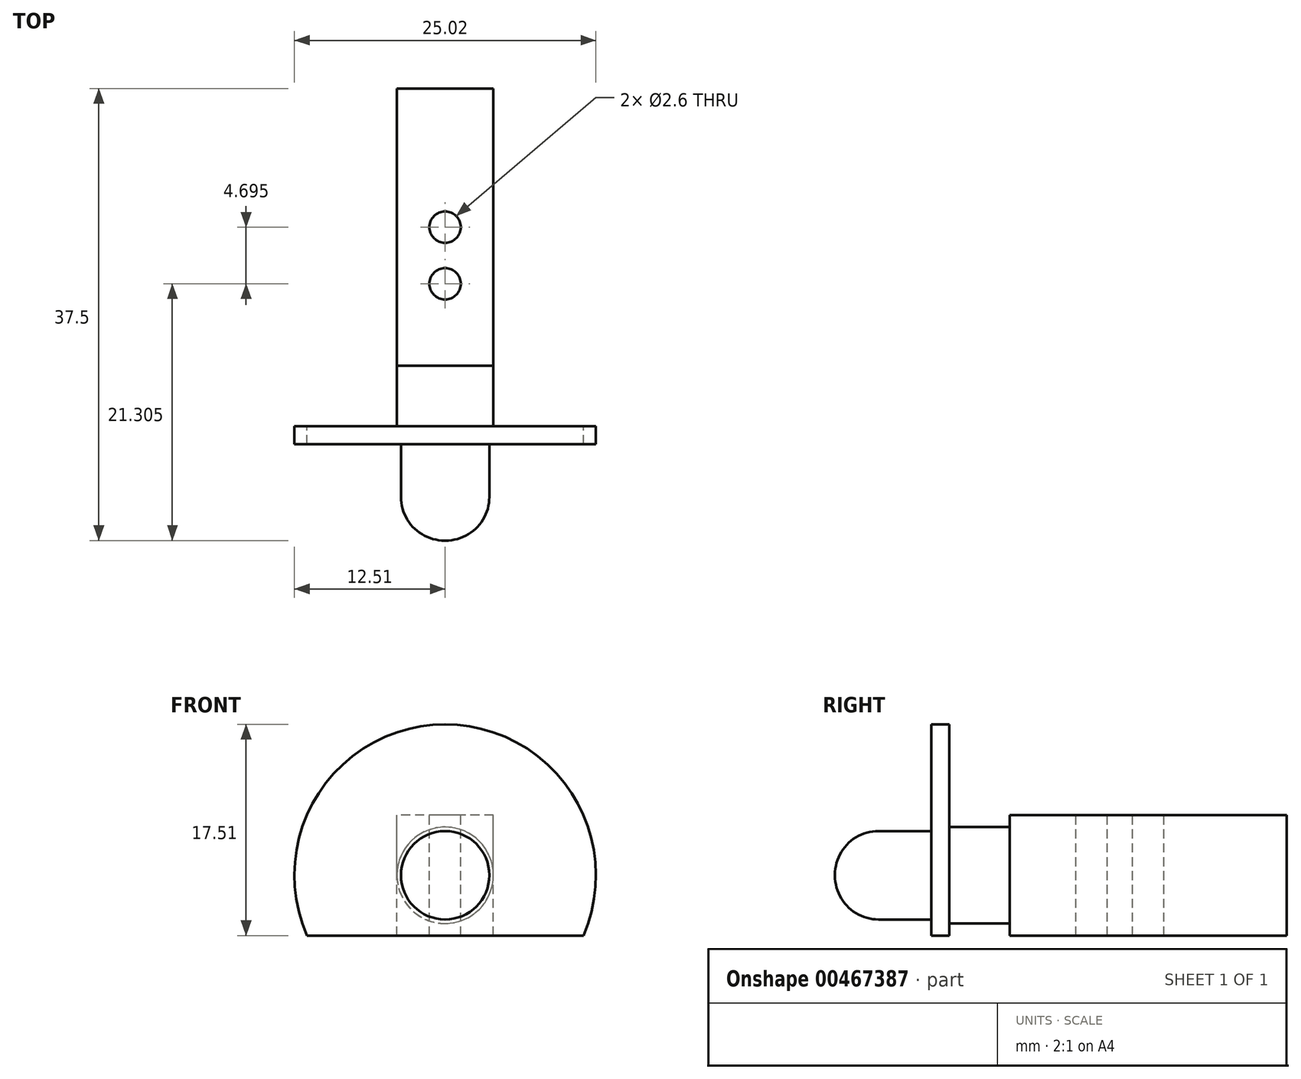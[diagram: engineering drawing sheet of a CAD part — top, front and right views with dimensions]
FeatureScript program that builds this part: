
annotation { "Feature Type Name" : "Feature", "Feature Type Description" : "" }
export const myFeature = defineFeature(function(context is Context, id is Id, definition is map)
    precondition{}
    {
        {
            var Q0;
            Q0=qCreatedBy(makeId("Right.planeOp"),FACE);
            var sketch = newSketch(context, id + "F0", { "sketchPlane" : qUnion([Q0])});
            skLineSegment(sketch, "E0.bottom", {"start": v(11.5, -5) * mm, "end": v(-11.5, -5) * mm});
            skLineSegment(sketch, "E0.top", {"start": v(11.5, 5) * mm, "end": v(-11.5, 5) * mm});
            skLineSegment(sketch, "E0.left", {"start": v(11.5, -5) * mm, "end": v(11.5, 5) * mm});
            skLineSegment(sketch, "E0.right", {"start": v(-11.5, -5) * mm, "end": v(-11.5, 5) * mm});
            skPoint(sketch, "E0.middle", {"position": v(0, 0) * mm});
            skSolve(sketch);
        }
        {
            var Q0;
            Q0 = qSketchRegion(id + "F0", true);
            extrude(context, id + "F1", {"entities" : qUnion([Q0]), "depth" : 8 * mm});
        }
        {
            var Q0;
            Q0=makeQuery(id+"F1.opExtrude","SWEPT_FACE",FACE,{"disambiguationData":[OSD([sQuery(id+"F0.wireOp",EDGE,"E0.right")])]});
            var sketch = newSketch(context, id + "F2", { "sketchPlane" : qUnion([Q0])});
            skLineSegment(sketch, "E1", {"start": v(0, 0) * mm, "end": v(4, 0) * mm});
            skCircle(sketch, "E2", {"center": v(4, 0) * mm, "radius": 4 * mm});
            skSolve(sketch);
        }
        {
            var Q0;
            Q0 = qSketchRegion(id + "F2", true);
            extrude(context, id + "F3", {"entities" : qUnion([Q0]), "operationType" : NewBodyOperationType.ADD, "depth" : 5 * mm});
        }
        {
            var Q0;
            Q0=makeQuery(id+"F3.opExtrude","CAP_FACE",FACE,{"disambiguationData":[OSD([sQuery(id+"F2.wireOp",EDGE,"E2")])],"isStart":false});
            var sketch = newSketch(context, id + "F4", { "sketchPlane" : qUnion([Q0])});
            skCircle(sketch, "E3", {"center": v(4, 0) * mm, "radius": 12.51 * mm});
            skSolve(sketch);
        }
        {
            var Q0;
            Q0 = qSketchRegion(id + "F4", true);
            extrude(context, id + "F5", {"entities" : qUnion([Q0]), "operationType" : NewBodyOperationType.ADD, "depth" : 1.5 * mm});
        }
        {
            var Q0;
            Q0=makeQuery(id+"F5.opExtrude","CAP_FACE",FACE,{"disambiguationData":[OSD([sQuery(id+"F4.wireOp",EDGE,"E3")])],"isStart":false});
            var sketch = newSketch(context, id + "F6", { "sketchPlane" : qUnion([Q0])});
            skCircle(sketch, "E4", {"center": v(4, 0) * mm, "radius": 3.67 * mm});
            skSolve(sketch);
        }
        {
            var Q0;
            Q0 = qSketchRegion(id + "F6", true);
            extrude(context, id + "F7", {"entities" : qUnion([Q0]), "operationType" : NewBodyOperationType.ADD, "depth" : 8 * mm});
        }
        {
            var Q0;
            Q0=makeQuery(id+"F7.opExtrude","CAP_FACE",FACE,{"disambiguationData":[OSD([sQuery(id+"F6.wireOp",EDGE,"E4")])],"isStart":false});
            fillet(context, id + "F8", {"entities" : qUnion([Q0]), "radius" : 3.62 * mm, "tangentPropagation" : true, "allowEdgeOverflow" : false});
        }
        {
            var Q0;
            Q0=makeQuery(id+"F1.opExtrude","SWEPT_FACE",FACE,{"disambiguationData":[OSD([sQuery(id+"F0.wireOp",EDGE,"E0.top")])]});
            var sketch = newSketch(context, id + "F9", { "sketchPlane" : qUnion([Q0])});
            skLineSegment(sketch, "E5", {"start": v(4, -11.5) * mm, "end": v(4, 0) * mm});
            skPoint(sketch, "E5.endSnap0", {"position": v(4, 11.5) * mm});
            skCircle(sketch, "E6", {"center": v(4, 0) * mm, "radius": 1.3 * mm});
            skSolve(sketch);
        }
        {
            var Q0;
            Q0 = qSketchRegion(id + "F9", true);
            extrude(context, id + "F10", {"entities" : qUnion([Q0]), "operationType" : NewBodyOperationType.REMOVE, "oppositeDirection" : true, "depth" : 25 * mm});
        }
        {
            var Q0;
            Q0=makeQuery(id+"F1.opExtrude","SWEPT_FACE",FACE,{"disambiguationData":[OSD([sQuery(id+"F0.wireOp",EDGE,"E0.top")])]});
            var sketch = newSketch(context, id + "F11", { "sketchPlane" : qUnion([Q0])});
            skLineSegment(sketch, "E7", {"start": v(4, -11.5) * mm, "end": v(4, -4.7) * mm});
            skCircle(sketch, "E8", {"center": v(4, -4.7) * mm, "radius": 1.3 * mm});
            skSolve(sketch);
        }
        {
            var Q0;
            {var subQ0=sQuery(id+"F0.wireOp",EDGE,"E0.top");var subQ2=makeQuery(id+"F1.opExtrude","CAP_EDGE",EDGE,{"disambiguationData":[OSD([subQ0])],"isStart":true});Q0=makeQuery(id+"F11.imprint","IMPRINT",FACE,{"disambiguationData":[TD([[makeQuery(id+"F11.imprint","IMPRINT",EDGE,{"derivedFrom":subQ2}),1.0]])]});}
            var sketch = newSketch(context, id + "F12", { "sketchPlane" : qUnion([Q0])});
            skSolve(sketch);
        }
        {
            var Q0;
            Q0 = qSketchRegion(id + "F11", true);
            extrude(context, id + "F13", {"entities" : qUnion([Q0]), "operationType" : NewBodyOperationType.REMOVE, "oppositeDirection" : true, "depth" : 25 * mm});
        }
        {
            var Q0;
            Q0=makeQuery(id+"F1.opExtrude","SWEPT_FACE",FACE,{"disambiguationData":[OSD([sQuery(id+"F0.wireOp",EDGE,"E0.bottom")])]});
            var sketch = newSketch(context, id + "F14", { "sketchPlane" : qUnion([Q0])});
            skLineSegment(sketch, "E9.bottom", {"start": v(18.09, 20.38) * mm, "end": v(-10.47, 20.38) * mm});
            skLineSegment(sketch, "E9.top", {"start": v(18.09, 14.04) * mm, "end": v(-10.47, 14.04) * mm});
            skLineSegment(sketch, "E9.left", {"start": v(18.09, 20.38) * mm, "end": v(18.09, 14.04) * mm});
            skLineSegment(sketch, "E9.right", {"start": v(-10.47, 20.38) * mm, "end": v(-10.47, 14.04) * mm});
            skSolve(sketch);
        }
        {
            var Q0;
            Q0 = qSketchRegion(id + "F14", true);
            extrude(context, id + "F15", {"entities" : qUnion([Q0]), "operationType" : NewBodyOperationType.REMOVE, "depth" : 9.5 * mm});
        }
    });
